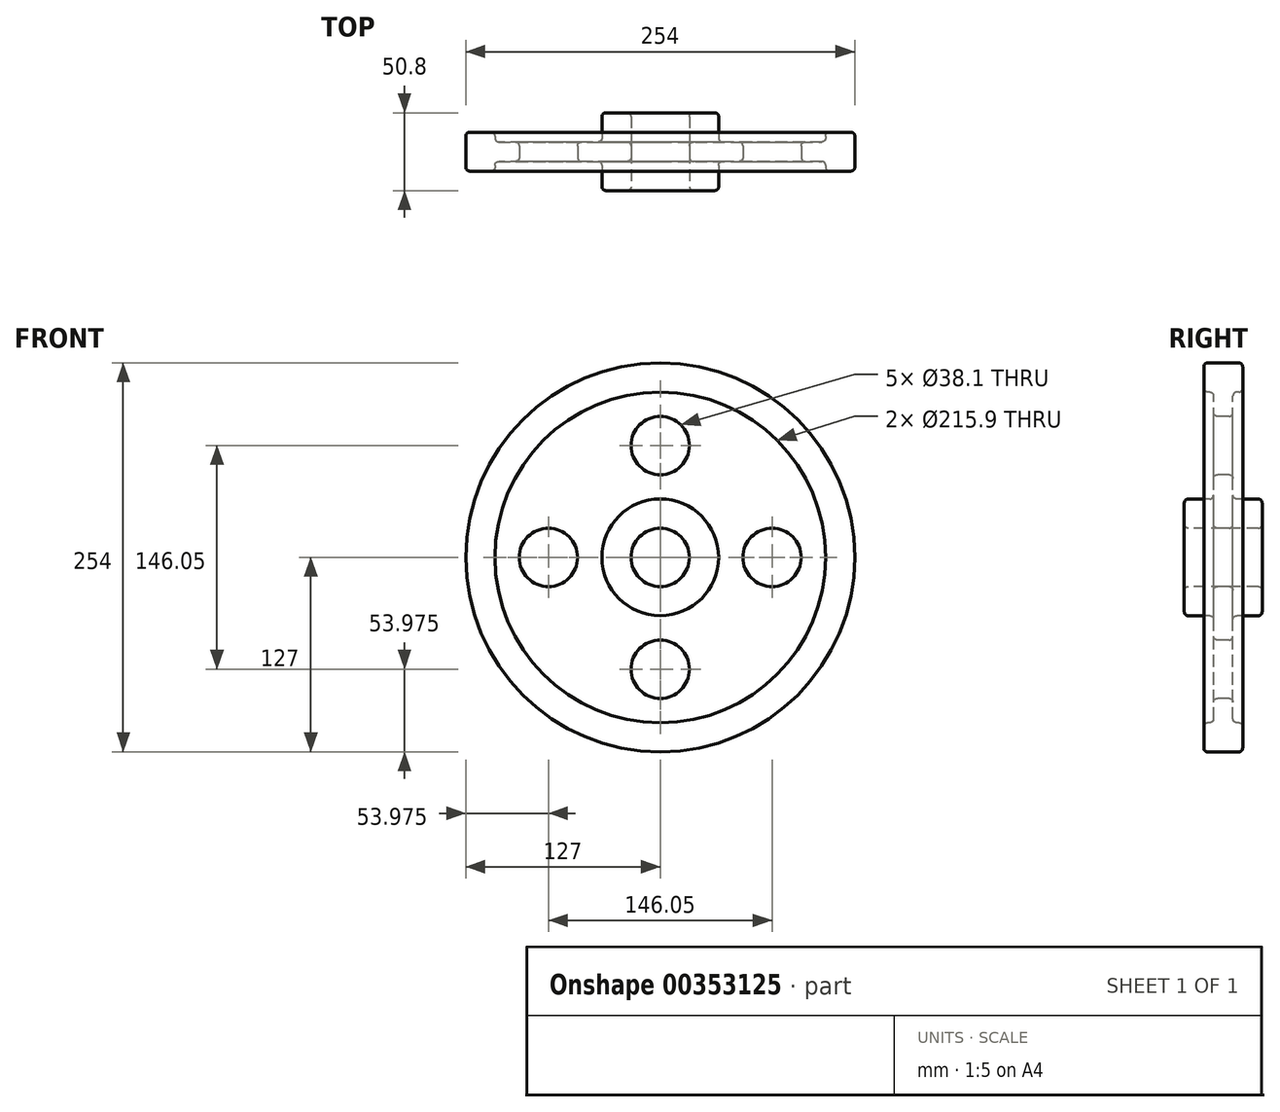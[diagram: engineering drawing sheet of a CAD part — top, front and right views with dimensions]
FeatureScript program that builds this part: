
annotation { "Feature Type Name" : "Feature", "Feature Type Description" : "" }
export const myFeature = defineFeature(function(context is Context, id is Id, definition is map)
    precondition{}
    {
        {
            var Q0;
            Q0=qCreatedBy(makeId("Right.planeOp"),FACE);
            var sketch = newSketch(context, id + "F0", { "sketchPlane" : qUnion([Q0])});
            skLineSegment(sketch, "E0.0", {"start": v(6.35, 19.05) * mm, "end": v(25.4, 19.05) * mm});
            skLineSegment(sketch, "E1.0", {"start": v(6.35, 38.1) * mm, "end": v(25.4, 38.1) * mm});
            skLineSegment(sketch, "E2.0", {"start": v(6.35, 107.95) * mm, "end": v(12.7, 107.95) * mm});
            skLineSegment(sketch, "E3.0", {"start": v(25.4, 19.05) * mm, "end": v(25.4, 38.1) * mm});
            skLineSegment(sketch, "E4.0", {"start": v(6.35, 127) * mm, "end": v(12.7, 127) * mm});
            skLineSegment(sketch, "E5.trimOffspring", {"start": v(12.7, 107.95) * mm, "end": v(12.7, 127) * mm});
            skLineSegment(sketch, "E6.trimOffspring", {"start": v(6.35, 38.1) * mm, "end": v(6.35, 107.95) * mm});
            skLineSegment(sketch, "E7", {"start": v(0, 127) * mm, "end": v(12.7, 127) * mm});
            skLineSegment(sketch, "E8.MirrorCS", {"start": v(-6.35, 107.95) * mm, "end": v(-12.7, 107.95) * mm});
            skLineSegment(sketch, "E9.MirrorCS", {"start": v(0, 127) * mm, "end": v(-12.7, 127) * mm});
            skLineSegment(sketch, "E10.MirrorCS", {"start": v(-6.35, 127) * mm, "end": v(-12.7, 127) * mm});
            skLineSegment(sketch, "E11.MirrorCS", {"start": v(-6.35, 19.05) * mm, "end": v(-25.4, 19.05) * mm});
            skLineSegment(sketch, "E12.MirrorCS", {"start": v(-6.35, 38.1) * mm, "end": v(-25.4, 38.1) * mm});
            skLineSegment(sketch, "E13.MirrorCS", {"start": v(-25.4, 19.05) * mm, "end": v(-25.4, 38.1) * mm});
            skLineSegment(sketch, "E14.MirrorCS", {"start": v(-12.7, 107.95) * mm, "end": v(-12.7, 127) * mm});
            skLineSegment(sketch, "E15.MirrorCS", {"start": v(-6.35, 38.1) * mm, "end": v(-6.35, 107.95) * mm});
            skPoint(sketch, "E16.MirrorCS.end.orphan", {"position": v(-12.7, 19.05) * mm});
            skPoint(sketch, "E16.MirrorCS.start.orphan", {"position": v(-12.7, 0) * mm});
            skPoint(sketch, "E17.0.end.orphan", {"position": v(12.7, 19.05) * mm});
            skPoint(sketch, "E17.0.start.orphan", {"position": v(12.7, 0) * mm});
            skPoint(sketch, "E18.orphan", {"position": v(-25.4, 0) * mm});
            skPoint(sketch, "E19.MirrorCS.start.orphan", {"position": v(-6.35, 0) * mm});
            skPoint(sketch, "E20.orphan", {"position": v(25.4, 0) * mm});
            skPoint(sketch, "E21.start.orphan", {"position": v(6.35, 0) * mm});
            skLineSegment(sketch, "E22", {"start": v(-6.35, 19.05) * mm, "end": v(6.35, 19.05) * mm});
            skLineSegment(sketch, "E23", {"start": v(-25.4, 0) * mm, "end": v(25.4, 0) * mm, "construction": true});
            skSolve(sketch);
        }
        {
            var Q0;
            Q0=makeQuery(id+"F0.imprint","IMPRINT",FACE,{"disambiguationData":[TD([[makeQuery(id+"F0.imprint","IMPRINT",EDGE,{"derivedFrom":sQuery(id+"F0.wireOp",EDGE,"E0.0")}),1.0]])]});
            var Q1;
            Q1=sQuery(id+"F0.wireOp",EDGE,"E23");
            revolve(context, id + "F1", {"entities" : qUnion([Q0]), "axis" : qUnion([Q1]), "revolveType" : RevolveType.FULL});
        }
        {
            var Q0;
            Q0=makeQuery(id+"F1.opRevolve","SWEPT_FACE",FACE,{"disambiguationData":[OSD([sQuery(id+"F0.wireOp",EDGE,"E15.MirrorCS")])]});
            var sketch = newSketch(context, id + "F2", { "sketchPlane" : qUnion([Q0])});
            skLineSegment(sketch, "E24", {"start": v(0, 0) * mm, "end": v(0, 73.03) * mm});
            skCircle(sketch, "E25", {"center": v(0, 73.03) * mm, "radius": 19.05 * mm});
            skPoint(sketch, "E26.center", {"position": v(0, 0) * mm});
            skCircle(sketch, "E27.1.0", {"center": v(-73.03, 0) * mm, "radius": 19.05 * mm});
            skCircle(sketch, "E27.2.0", {"center": v(0, -73.03) * mm, "radius": 19.05 * mm});
            skCircle(sketch, "E27.3.0", {"center": v(73.03, 0) * mm, "radius": 19.05 * mm});
            skSolve(sketch);
        }
        {
            var Q0;
            Q0=makeQuery(id+"F2.imprint","IMPRINT",FACE,{"disambiguationData":[TD([[makeQuery(id+"F2.imprint","IMPRINT",EDGE,{"derivedFrom":sQuery(id+"F2.wireOp",EDGE,"E25")}),1.0]])]});
            var Q1;
            Q1=makeQuery(id+"F2.imprint","IMPRINT",FACE,{"disambiguationData":[TD([[makeQuery(id+"F2.imprint","IMPRINT",EDGE,{"derivedFrom":sQuery(id+"F2.wireOp",EDGE,"E27.3.0")}),1.0]])]});
            var Q2;
            Q2=makeQuery(id+"F2.imprint","IMPRINT",FACE,{"disambiguationData":[TD([[makeQuery(id+"F2.imprint","IMPRINT",EDGE,{"derivedFrom":sQuery(id+"F2.wireOp",EDGE,"E27.2.0")}),1.0]])]});
            var Q3;
            Q3=makeQuery(id+"F2.imprint","IMPRINT",FACE,{"disambiguationData":[TD([[makeQuery(id+"F2.imprint","IMPRINT",EDGE,{"derivedFrom":sQuery(id+"F2.wireOp",EDGE,"E27.1.0")}),1.0]])]});
            extrude(context, id + "F3", {"entities" : qUnion([Q0, Q1, Q2, Q3]), "operationType" : NewBodyOperationType.REMOVE, "oppositeDirection" : true, "depth" : 25.4 * mm});
        }
        {
            var Q0;
            Q0=makeQuery(id+"F1.opRevolve","SWEPT_FACE",FACE,{"disambiguationData":[OSD([sQuery(id+"F0.wireOp",EDGE,"E0.0"),sQuery(id+"F0.wireOp",EDGE,"E11.MirrorCS"),sQuery(id+"F0.wireOp",EDGE,"E22")])]});
            var Q1;
            Q1=makeQuery(id+"F1.opRevolve","SWEPT_FACE",FACE,{"disambiguationData":[OSD([sQuery(id+"F0.wireOp",EDGE,"E5.trimOffspring")])]});
            var Q2;
            Q2=makeQuery(id+"F1.opRevolve","SWEPT_EDGE",EDGE,{"disambiguationData":[OSD([sQuery(id+"F0.wireOp",EDGE,"E5.trimOffspring"),sQuery(id+"F0.wireOp",EDGE,"E7")])]});
            var Q3;
            Q3=makeQuery(id+"F1.opRevolve","SWEPT_EDGE",EDGE,{"disambiguationData":[OSD([sQuery(id+"F0.wireOp",EDGE,"E8.MirrorCS"),sQuery(id+"F0.wireOp",EDGE,"E15.MirrorCS")])]});
            var Q4;
            Q4=makeQuery(id+"F1.opRevolve","SWEPT_FACE",FACE,{"disambiguationData":[OSD([sQuery(id+"F0.wireOp",EDGE,"E7"),sQuery(id+"F0.wireOp",EDGE,"E9.MirrorCS")])]});
            var Q5;
            Q5=makeQuery(id+"F1.opRevolve","SWEPT_EDGE",EDGE,{"disambiguationData":[OSD([sQuery(id+"F0.wireOp",EDGE,"E8.MirrorCS"),sQuery(id+"F0.wireOp",EDGE,"E14.MirrorCS")])]});
            var Q6;
            Q6=makeQuery(id+"F1.opRevolve","SWEPT_FACE",FACE,{"disambiguationData":[OSD([sQuery(id+"F0.wireOp",EDGE,"E8.MirrorCS")])]});
            var Q7;
            Q7=makeQuery(id+"F1.opRevolve","SWEPT_EDGE",EDGE,{"disambiguationData":[OSD([sQuery(id+"F0.wireOp",EDGE,"E9.MirrorCS"),sQuery(id+"F0.wireOp",EDGE,"E14.MirrorCS")])]});
            var Q8;
            Q8=makeQuery(id+"F1.opRevolve","SWEPT_FACE",FACE,{"disambiguationData":[OSD([sQuery(id+"F0.wireOp",EDGE,"E12.MirrorCS")])]});
            var Q9;
            Q9=makeQuery(id+"F1.opRevolve","SWEPT_FACE",FACE,{"disambiguationData":[OSD([sQuery(id+"F0.wireOp",EDGE,"E13.MirrorCS")])]});
            var Q10;
            Q10=makeQuery(id+"F1.opRevolve","SWEPT_EDGE",EDGE,{"disambiguationData":[OSD([sQuery(id+"F0.wireOp",EDGE,"E12.MirrorCS"),sQuery(id+"F0.wireOp",EDGE,"E15.MirrorCS")])]});
            var Q11;
            Q11=makeQuery(id+"F1.opRevolve","SWEPT_FACE",FACE,{"disambiguationData":[OSD([sQuery(id+"F0.wireOp",EDGE,"E14.MirrorCS")])]});
            var Q12;
            Q12=makeQuery(id+"F1.opRevolve","SWEPT_EDGE",EDGE,{"disambiguationData":[OSD([sQuery(id+"F0.wireOp",EDGE,"E12.MirrorCS"),sQuery(id+"F0.wireOp",EDGE,"E13.MirrorCS")])]});
            var Q13;
            Q13=makeQuery(id+"F3.boolean.opBoolean","COPY",FACE,{"derivedFrom":makeQuery(id+"F3.opExtrude","SWEPT_FACE",FACE,{"disambiguationData":[OSD([sQuery(id+"F2.wireOp",EDGE,"E25")])]})});
            var Q14;
            Q14=makeQuery(id+"F3.boolean.opBoolean","COPY",FACE,{"derivedFrom":makeQuery(id+"F3.opExtrude","SWEPT_FACE",FACE,{"disambiguationData":[OSD([sQuery(id+"F2.wireOp",EDGE,"E27.1.0")])]})});
            var Q15;
            Q15=makeQuery(id+"F3.boolean.opBoolean","COPY",FACE,{"derivedFrom":makeQuery(id+"F3.opExtrude","SWEPT_FACE",FACE,{"disambiguationData":[OSD([sQuery(id+"F2.wireOp",EDGE,"E27.2.0")])]})});
            var Q16;
            Q16=makeQuery(id+"F3.boolean.opBoolean","COPY",FACE,{"derivedFrom":makeQuery(id+"F3.opExtrude","SWEPT_FACE",FACE,{"disambiguationData":[OSD([sQuery(id+"F2.wireOp",EDGE,"E27.3.0")])]})});
            var Q17;
            Q17=makeQuery(id+"F1.opRevolve","SWEPT_FACE",FACE,{"disambiguationData":[OSD([sQuery(id+"F0.wireOp",EDGE,"E15.MirrorCS")])]});
            var Q18;
            Q18=makeQuery(id+"F3.boolean.opBoolean","INTERSECT",EDGE,{"derivedFrom":[makeQuery(id+"F1.opRevolve","SWEPT_FACE",FACE,{"disambiguationData":[OSD([sQuery(id+"F0.wireOp",EDGE,"E6.trimOffspring")])]}),makeQuery(id+"F3.opExtrude","SWEPT_FACE",FACE,{"disambiguationData":[OSD([sQuery(id+"F2.wireOp",EDGE,"E27.2.0")])]})]});
            var Q19;
            Q19=makeQuery(id+"F1.opRevolve","SWEPT_EDGE",EDGE,{"disambiguationData":[OSD([sQuery(id+"F0.wireOp",EDGE,"E1.0"),sQuery(id+"F0.wireOp",EDGE,"E6.trimOffspring")])]});
            var Q20;
            Q20=makeQuery(id+"F1.opRevolve","SWEPT_FACE",FACE,{"disambiguationData":[OSD([sQuery(id+"F0.wireOp",EDGE,"E1.0")])]});
            var Q21;
            Q21=makeQuery(id+"F1.opRevolve","SWEPT_EDGE",EDGE,{"disambiguationData":[OSD([sQuery(id+"F0.wireOp",EDGE,"E1.0"),sQuery(id+"F0.wireOp",EDGE,"E3.0")])]});
            var Q22;
            Q22=makeQuery(id+"F1.opRevolve","SWEPT_FACE",FACE,{"disambiguationData":[OSD([sQuery(id+"F0.wireOp",EDGE,"E2.0")])]});
            var Q23;
            Q23=makeQuery(id+"F1.opRevolve","SWEPT_EDGE",EDGE,{"disambiguationData":[OSD([sQuery(id+"F0.wireOp",EDGE,"E2.0"),sQuery(id+"F0.wireOp",EDGE,"E6.trimOffspring")])]});
            var Q24;
            Q24=makeQuery(id+"F1.opRevolve","SWEPT_FACE",FACE,{"disambiguationData":[OSD([sQuery(id+"F0.wireOp",EDGE,"E3.0")])]});
            var Q25;
            Q25=makeQuery(id+"F1.opRevolve","SWEPT_EDGE",EDGE,{"disambiguationData":[OSD([sQuery(id+"F0.wireOp",EDGE,"E2.0"),sQuery(id+"F0.wireOp",EDGE,"E5.trimOffspring")])]});
            var Q26;
            Q26=makeQuery(id+"F1.opRevolve","SWEPT_EDGE",EDGE,{"disambiguationData":[OSD([sQuery(id+"F0.wireOp",EDGE,"E11.MirrorCS"),sQuery(id+"F0.wireOp",EDGE,"E13.MirrorCS")])]});
            var Q27;
            Q27=makeQuery(id+"F3.boolean.opBoolean","COPY",EDGE,{"derivedFrom":makeQuery(id+"F3.opExtrude","CAP_EDGE",EDGE,{"disambiguationData":[OSD([sQuery(id+"F2.wireOp",EDGE,"E25")])],"isStart":true})});
            var Q28;
            Q28=makeQuery(id+"F3.boolean.opBoolean","COPY",EDGE,{"derivedFrom":makeQuery(id+"F3.opExtrude","CAP_EDGE",EDGE,{"disambiguationData":[OSD([sQuery(id+"F2.wireOp",EDGE,"E27.1.0")])],"isStart":true})});
            var Q29;
            Q29=makeQuery(id+"F3.boolean.opBoolean","COPY",EDGE,{"derivedFrom":makeQuery(id+"F3.opExtrude","CAP_EDGE",EDGE,{"disambiguationData":[OSD([sQuery(id+"F2.wireOp",EDGE,"E27.2.0")])],"isStart":true})});
            var Q30;
            Q30=makeQuery(id+"F3.boolean.opBoolean","COPY",EDGE,{"derivedFrom":makeQuery(id+"F3.opExtrude","CAP_EDGE",EDGE,{"disambiguationData":[OSD([sQuery(id+"F2.wireOp",EDGE,"E27.3.0")])],"isStart":true})});
            var Q31;
            Q31=makeQuery(id+"F1.opRevolve","SWEPT_FACE",FACE,{"disambiguationData":[OSD([sQuery(id+"F0.wireOp",EDGE,"E6.trimOffspring")])]});
            var Q32;
            Q32=makeQuery(id+"F3.boolean.opBoolean","INTERSECT",EDGE,{"derivedFrom":[makeQuery(id+"F1.opRevolve","SWEPT_FACE",FACE,{"disambiguationData":[OSD([sQuery(id+"F0.wireOp",EDGE,"E6.trimOffspring")])]}),makeQuery(id+"F3.opExtrude","SWEPT_FACE",FACE,{"disambiguationData":[OSD([sQuery(id+"F2.wireOp",EDGE,"E27.1.0")])]})]});
            var Q33;
            Q33=makeQuery(id+"F3.boolean.opBoolean","INTERSECT",EDGE,{"derivedFrom":[makeQuery(id+"F1.opRevolve","SWEPT_FACE",FACE,{"disambiguationData":[OSD([sQuery(id+"F0.wireOp",EDGE,"E6.trimOffspring")])]}),makeQuery(id+"F3.opExtrude","SWEPT_FACE",FACE,{"disambiguationData":[OSD([sQuery(id+"F2.wireOp",EDGE,"E27.3.0")])]})]});
            var Q34;
            Q34=makeQuery(id+"F1.opRevolve","SWEPT_EDGE",EDGE,{"disambiguationData":[OSD([sQuery(id+"F0.wireOp",EDGE,"E0.0"),sQuery(id+"F0.wireOp",EDGE,"E3.0")])]});
            var Q35;
            Q35=makeQuery(id+"F3.boolean.opBoolean","INTERSECT",EDGE,{"derivedFrom":[makeQuery(id+"F1.opRevolve","SWEPT_FACE",FACE,{"disambiguationData":[OSD([sQuery(id+"F0.wireOp",EDGE,"E6.trimOffspring")])]}),makeQuery(id+"F3.opExtrude","SWEPT_FACE",FACE,{"disambiguationData":[OSD([sQuery(id+"F2.wireOp",EDGE,"E25")])]})]});
            fillet(context, id + "F4", {"entities" : qUnion([Q0, Q1, Q2, Q3, Q4, Q5, Q6, Q7, Q8, Q9, Q10, Q11, Q12, Q13, Q14, Q15, Q16, Q17, Q18, Q19, Q20, Q21, Q22, Q23, Q24, Q25, Q26, Q27, Q28, Q29, Q30, Q31, Q32, Q33, Q34, Q35]), "radius" : 2.54 * mm, "tangentPropagation" : true, "allowEdgeOverflow" : false});
        }
    });
